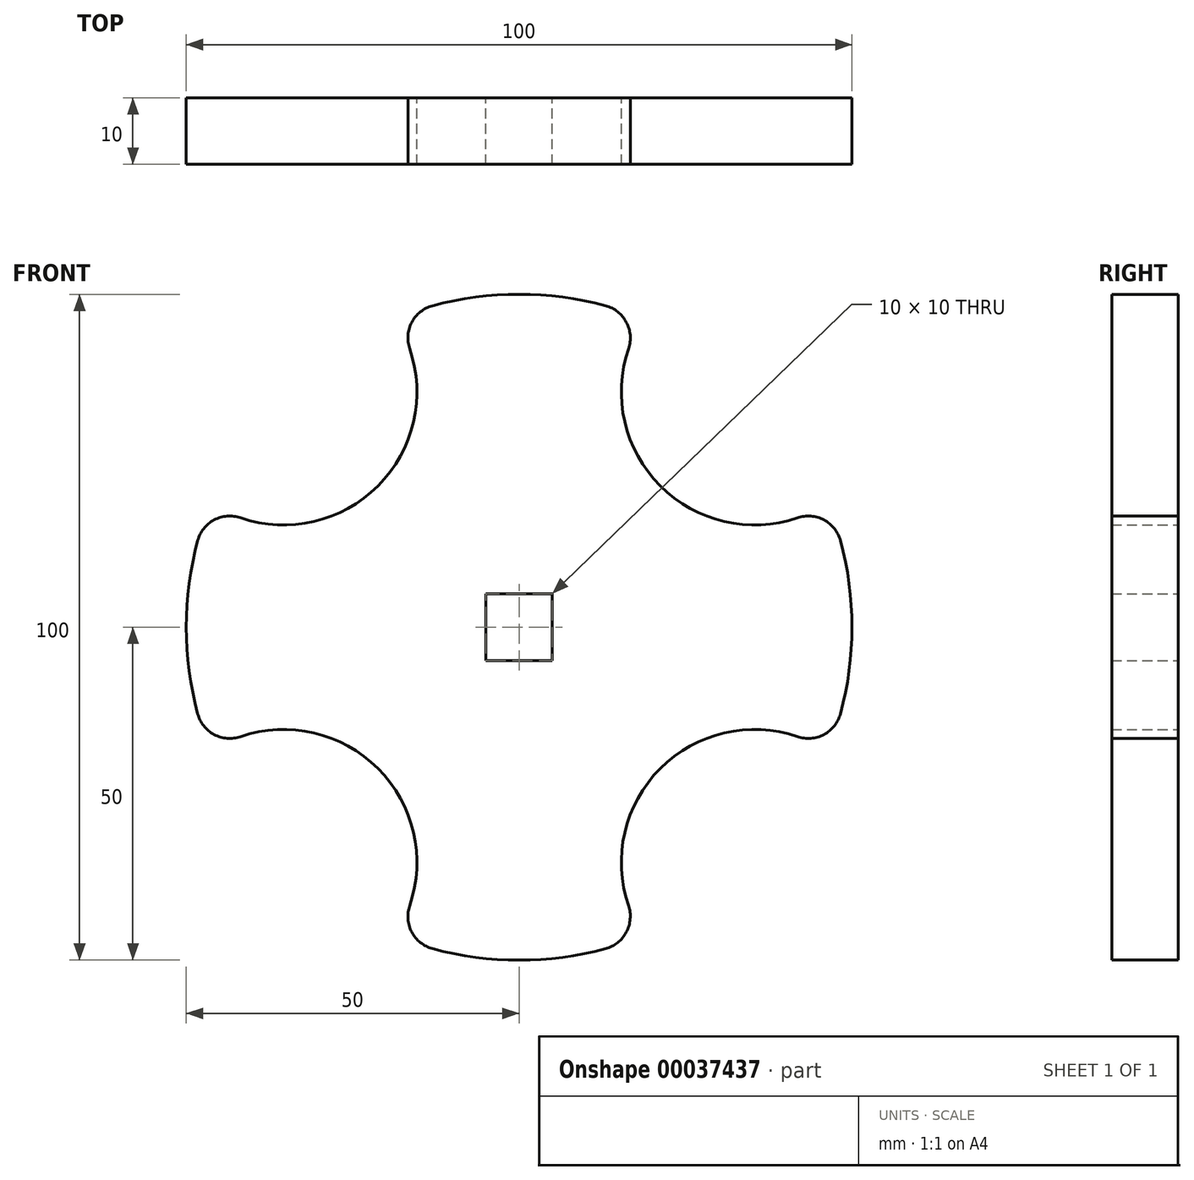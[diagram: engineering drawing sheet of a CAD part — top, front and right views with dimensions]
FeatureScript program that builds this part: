
annotation { "Feature Type Name" : "Feature", "Feature Type Description" : "" }
export const myFeature = defineFeature(function(context is Context, id is Id, definition is map)
    precondition{}
    {
        {
            var Q0;
            Q0=qCreatedBy(makeId("Front.planeOp"),FACE);
            var sketch = newSketch(context, id + "F0", { "sketchPlane" : qUnion([Q0])});
            skCircle(sketch, "E0", {"center": v(0, 0) * mm, "radius": 50 * mm});
            skLineSegment(sketch, "E1.rect.bottom", {"start": v(-5, 5) * mm, "end": v(5, 5) * mm});
            skLineSegment(sketch, "E1.rect.top", {"start": v(-5, -5) * mm, "end": v(5, -5) * mm});
            skLineSegment(sketch, "E1.rect.left", {"start": v(-5, 5) * mm, "end": v(-5, -5) * mm});
            skLineSegment(sketch, "E1.rect.right", {"start": v(5, 5) * mm, "end": v(5, -5) * mm});
            skLineSegment(sketch, "E2", {"start": v(0, 0) * mm, "end": v(35.36, 35.36) * mm, "construction": true});
            skLineSegment(sketch, "E3", {"start": v(0, 0) * mm, "end": v(-35.36, 35.36) * mm, "construction": true});
            skLineSegment(sketch, "E4", {"start": v(0, 0) * mm, "end": v(-56.03, 0) * mm, "construction": true});
            skCircle(sketch, "E5", {"center": v(-35.36, 35.36) * mm, "radius": 20 * mm});
            skCircle(sketch, "E6", {"center": v(35.36, 35.36) * mm, "radius": 20 * mm});
            skCircle(sketch, "E7.MirrorC", {"center": v(-35.36, -35.36) * mm, "radius": 20 * mm});
            skCircle(sketch, "E8.MirrorC", {"center": v(35.36, -35.36) * mm, "radius": 20 * mm});
            skSolve(sketch);
        }
        {
            var Q0;
            Q0=makeQuery(id+"F0.imprint","IMPRINT",FACE,{"disambiguationData":[TD([[makeQuery(id+"F0.imprint","IMPRINT",EDGE,{"derivedFrom":sQuery(id+"F0.wireOp",EDGE,"E1.rect.bottom")}),1.0]])]});
            extrude(context, id + "F1", {"entities" : qUnion([Q0]), "depth" : 10 * mm});
        }
        {
            var Q0;
            {var subQ0=sQuery(id+"F0.wireOp",EDGE,"E0");var subQ1=sQuery(id+"F0.wireOp",EDGE,"E5");Q0=makeQuery(id+"F1.opExtrude","SWEPT_EDGE",EDGE,{"disambiguationData":[OSD([subQ0,subQ1]),TDD([makeQuery(id+"F0.imprint","INTERSECT",VERTEX,{"disambiguationData":[OD(1.0)],"derivedFrom":[subQ0,subQ1]})])]});}
            var Q1;
            {var subQ0=sQuery(id+"F0.wireOp",EDGE,"E0");var subQ1=sQuery(id+"F0.wireOp",EDGE,"E5");Q1=makeQuery(id+"F1.opExtrude","SWEPT_EDGE",EDGE,{"disambiguationData":[OSD([subQ0,subQ1]),TDD([makeQuery(id+"F0.imprint","INTERSECT",VERTEX,{"disambiguationData":[OD(0.0)],"derivedFrom":[subQ0,subQ1]})])]});}
            var Q2;
            {var subQ0=sQuery(id+"F0.wireOp",EDGE,"E0");var subQ1=sQuery(id+"F0.wireOp",EDGE,"E6");Q2=makeQuery(id+"F1.opExtrude","SWEPT_EDGE",EDGE,{"disambiguationData":[OSD([subQ0,subQ1]),TDD([makeQuery(id+"F0.imprint","INTERSECT",VERTEX,{"disambiguationData":[OD(0.0)],"derivedFrom":[subQ0,subQ1]})])]});}
            var Q3;
            {var subQ0=sQuery(id+"F0.wireOp",EDGE,"E0");var subQ1=sQuery(id+"F0.wireOp",EDGE,"E6");Q3=makeQuery(id+"F1.opExtrude","SWEPT_EDGE",EDGE,{"disambiguationData":[OSD([subQ0,subQ1]),TDD([makeQuery(id+"F0.imprint","INTERSECT",VERTEX,{"disambiguationData":[OD(1.0)],"derivedFrom":[subQ0,subQ1]})])]});}
            fillet(context, id + "F2", {"entities" : qUnion([Q0, Q1, Q2, Q3]), "radius" : 5 * mm, "tangentPropagation" : true, "allowEdgeOverflow" : false});
        }
        {
            var Q0;
            {var subQ0=sQuery(id+"F0.wireOp",EDGE,"E0");var subQ1=sQuery(id+"F0.wireOp",EDGE,"E7.MirrorC");Q0=makeQuery(id+"F1.opExtrude","SWEPT_EDGE",EDGE,{"disambiguationData":[OSD([subQ0,subQ1]),TDD([makeQuery(id+"F0.imprint","INTERSECT",VERTEX,{"disambiguationData":[OD(1.0)],"derivedFrom":[subQ0,subQ1]})])]});}
            var Q1;
            {var subQ0=sQuery(id+"F0.wireOp",EDGE,"E0");var subQ1=sQuery(id+"F0.wireOp",EDGE,"E7.MirrorC");Q1=makeQuery(id+"F1.opExtrude","SWEPT_EDGE",EDGE,{"disambiguationData":[OSD([subQ0,subQ1]),TDD([makeQuery(id+"F0.imprint","INTERSECT",VERTEX,{"disambiguationData":[OD(0.0)],"derivedFrom":[subQ0,subQ1]})])]});}
            var Q2;
            {var subQ0=sQuery(id+"F0.wireOp",EDGE,"E0");var subQ1=sQuery(id+"F0.wireOp",EDGE,"E8.MirrorC");Q2=makeQuery(id+"F1.opExtrude","SWEPT_EDGE",EDGE,{"disambiguationData":[OSD([subQ0,subQ1]),TDD([makeQuery(id+"F0.imprint","INTERSECT",VERTEX,{"disambiguationData":[OD(0.0)],"derivedFrom":[subQ0,subQ1]})])]});}
            var Q3;
            {var subQ0=sQuery(id+"F0.wireOp",EDGE,"E0");var subQ1=sQuery(id+"F0.wireOp",EDGE,"E8.MirrorC");Q3=makeQuery(id+"F1.opExtrude","SWEPT_EDGE",EDGE,{"disambiguationData":[OSD([subQ0,subQ1]),TDD([makeQuery(id+"F0.imprint","INTERSECT",VERTEX,{"disambiguationData":[OD(1.0)],"derivedFrom":[subQ0,subQ1]})])]});}
            fillet(context, id + "F3", {"entities" : qUnion([Q0, Q1, Q2, Q3]), "radius" : 5 * mm, "tangentPropagation" : true, "allowEdgeOverflow" : false});
        }
    });
